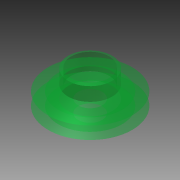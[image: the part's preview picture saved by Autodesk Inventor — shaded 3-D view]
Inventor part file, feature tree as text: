
AUTODESK INVENTOR PART (.ipt)
format: ipt  version: 2011 (Build 150239000, 239)  size: 119,296 bytes
history: native  units: in
note: dims shown in document units (in); Inventor stores cm internally (conversion verified against a paired STEP export)
features: revolve x1, plane x1, sketch x1
ambient origin geometry x8: Origin, YZ Plane, XZ Plane, XY Plane, X Axis, Y Axis, Z Axis, Center Point
bodies: Solid1 (feature_tree)
feature tree (3):
  revolve  "Revolution1"  [1 undecoded]
  plane  "Work Plane1"
  sketch  "Sketch1"  dims[d1=0.5in d2=0.5in d3=0.325in d4=0.075in d7=1.0in d8=90.0deg d10=0.9375in]
note: 1 required parameter value undecoded (feature->parameter linkage not recoverable at this tier; creation-order binding heuristic only, values carry confidence <= 0.55)
